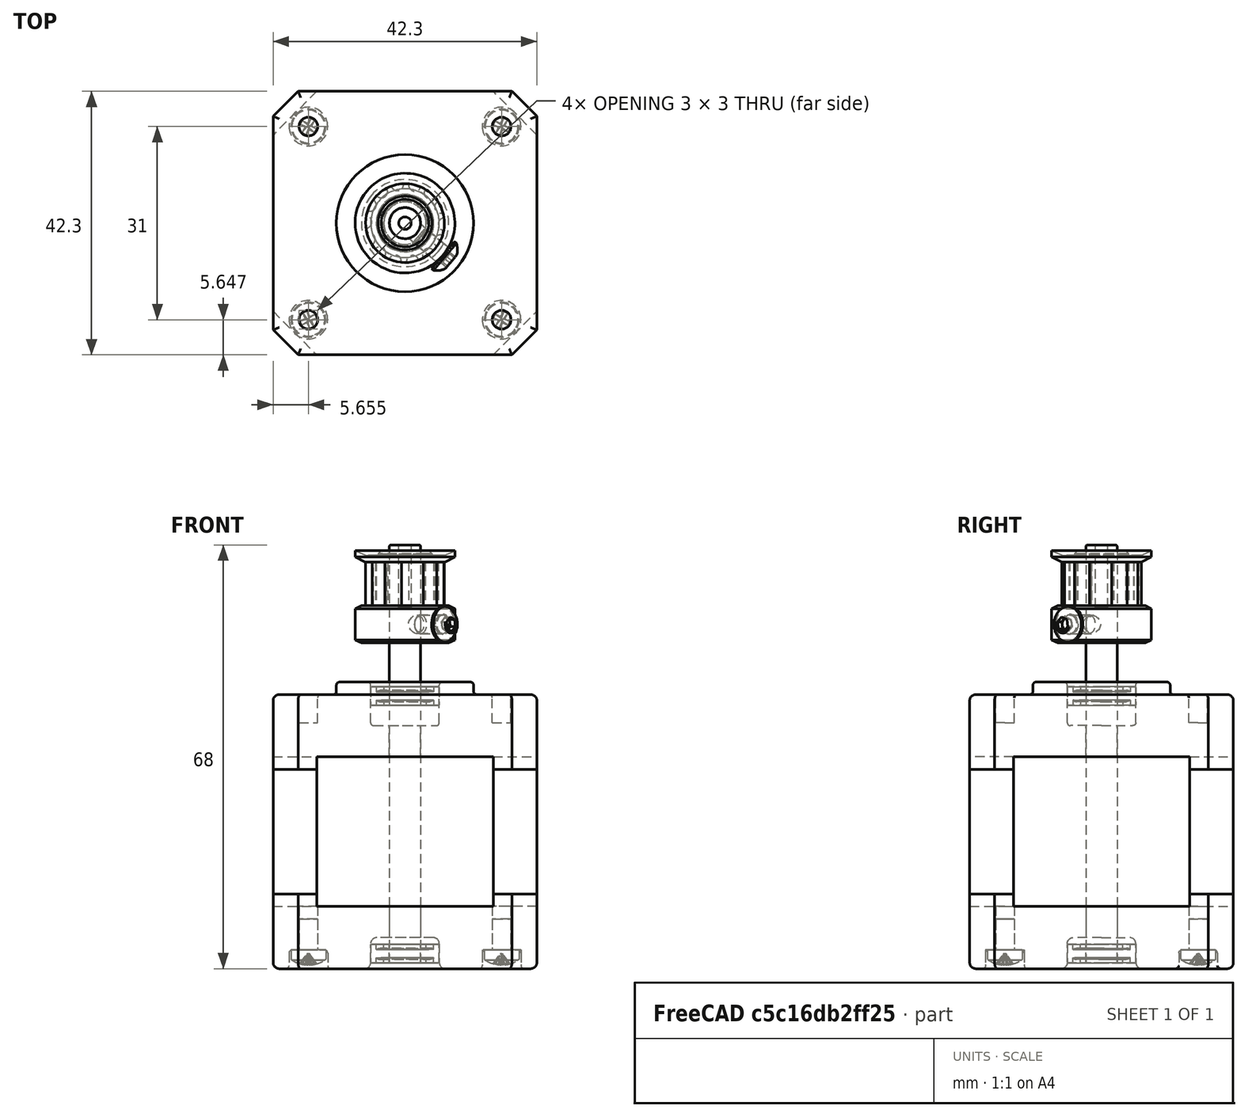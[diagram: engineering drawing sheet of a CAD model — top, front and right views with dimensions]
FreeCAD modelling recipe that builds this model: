
FCSTD DOCUMENT  (FreeCAD 2022.430R26244 +4758 (Git))
Label: As3NEMA 17
License: All rights reserved
LicenseURL: http://en.wikipedia.org/wiki/All_rights_reserved
objects: Part::FeaturePython×4, App::FeaturePython×2, Part::Feature×1
note: 4 computed .brp shape members not serialized (recipe doc carries the construction recipe); baked Part::Feature solids carry a one-line shape summary decoded from their .brp

FEATURE [Part::Feature] Feature  label="NEMA 17 with T5 Pulley001"
  TreeRank = 0
  shape: bbox 42.3 x 42.3 x 68 mm, 443 faces, 12 solids (baked)
FEATURE [App::FeaturePython] Constraints  # WARN: FeaturePython — macro-defined, semantics opaque (R4)
  TreeRank = 0
  _LinkVersion = 1
  _Version = 1
FEATURE [Part::FeaturePython] Parts  # WARN: FeaturePython — macro-defined, semantics opaque (R4)
  Group = -> [Feature]
  GroupMode = 0
  TreeRank = 0
  _LinkVersion = 1
FEATURE [Part::FeaturePython] Assembly  label="As3NEMA 17"  # WARN: FeaturePython — macro-defined, semantics opaque (R4)
  AutoRelax = true
  BuildShape = 0
  Freeze = false
  Group = -> [Constraints,Elements,Parts]
  TreeRank = 0
  Verbose = false
  _LinkVersion = 1
  _SolverType = 1
  _Version = 1
FEATURE [App::FeaturePython] Elements  # WARN: FeaturePython — macro-defined, semantics opaque (R4)
  Group = -> [Element,Element001]
  TreeRank = 0
  _LinkVersion = 1
FEATURE [Part::FeaturePython] Element  label="CentreMot"  # link proxy (typed FeaturePython)
  Detach = false
  LinkTransform = true
  LinkedObject = -> Feature [Edge247]
  TreeRank = 0
  _LinkVersion = 1
  _Parent = -> Elements
FEATURE [Part::FeaturePython] Element001  label="FaceH"  # link proxy (typed FeaturePython)
  Detach = false
  LinkTransform = true
  LinkedObject = -> Feature [Face103]
  TreeRank = 0
  _LinkVersion = 1
  _Parent = -> Elements
